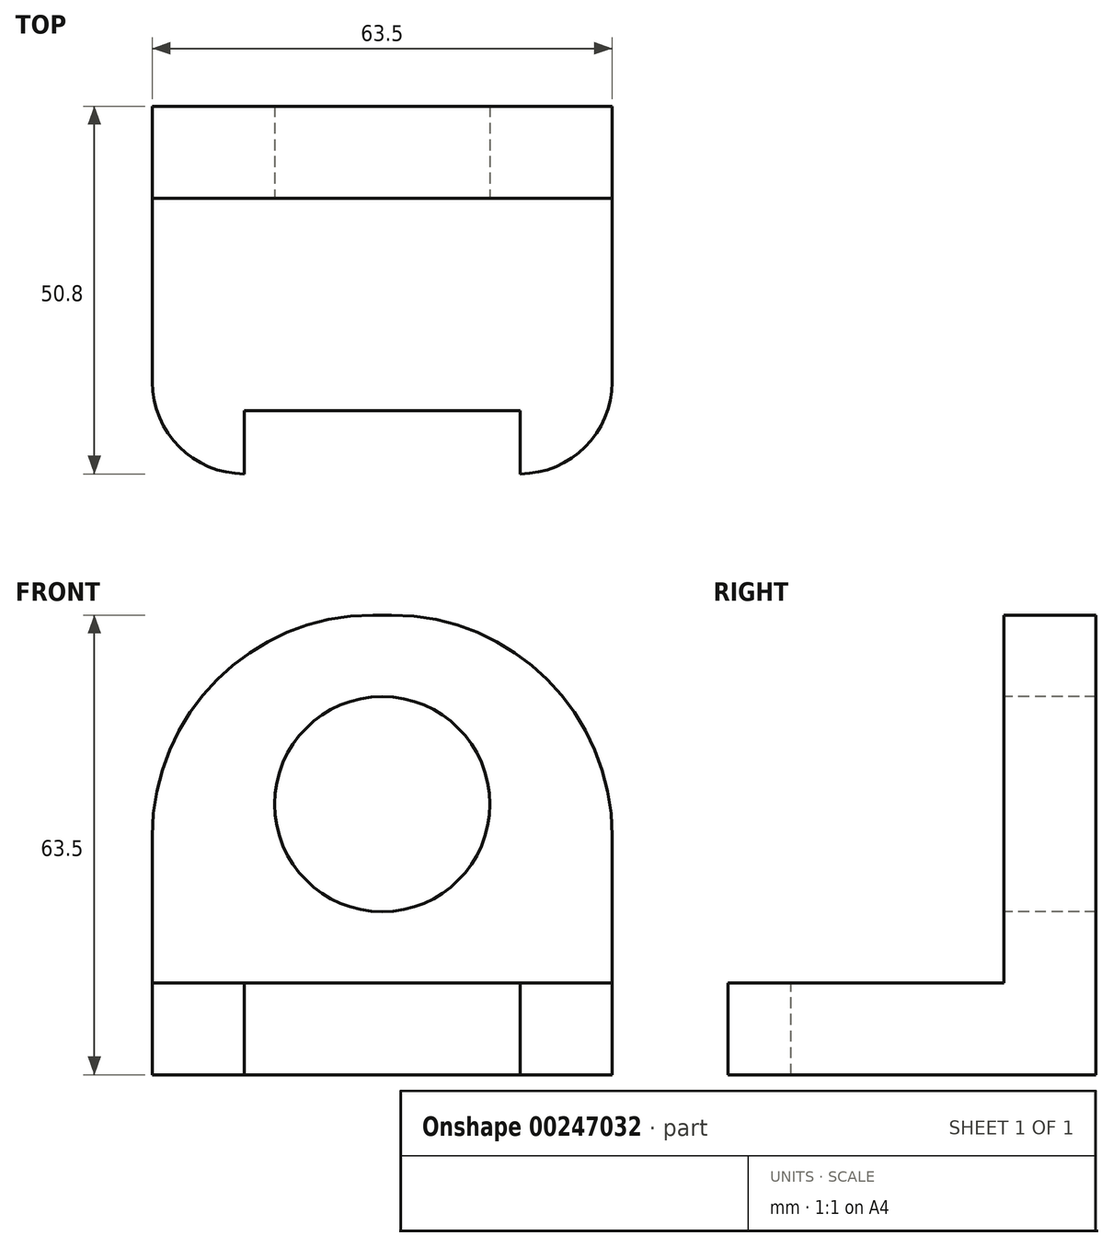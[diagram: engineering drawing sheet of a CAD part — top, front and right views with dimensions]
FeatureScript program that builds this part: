
annotation { "Feature Type Name" : "Feature", "Feature Type Description" : "" }
export const myFeature = defineFeature(function(context is Context, id is Id, definition is map)
    precondition{}
    {
        {
            var Q0;
            Q0=qCreatedBy(makeId("Right.planeOp"),FACE);
            var sketch = newSketch(context, id + "F0", { "sketchPlane" : qUnion([Q0])});
            skLineSegment(sketch, "E0", {"start": v(0, 0) * mm, "end": v(0, 63.5) * mm});
            skLineSegment(sketch, "E1", {"start": v(0, 63.5) * mm, "end": v(-12.7, 63.5) * mm});
            skLineSegment(sketch, "E2", {"start": v(-12.7, 63.5) * mm, "end": v(-12.7, 12.7) * mm});
            skLineSegment(sketch, "E3", {"start": v(-12.7, 12.7) * mm, "end": v(-50.8, 12.7) * mm});
            skLineSegment(sketch, "E4", {"start": v(-50.8, 12.7) * mm, "end": v(-50.8, 0) * mm});
            skLineSegment(sketch, "E5", {"start": v(-50.8, 0) * mm, "end": v(0, 0) * mm});
            skSolve(sketch);
        }
        {
            var Q0;
            Q0=makeQuery(id+"F0.imprint","IMPRINT",FACE,{"disambiguationData":[TD([[makeQuery(id+"F0.imprint","IMPRINT",EDGE,{"derivedFrom":sQuery(id+"F0.wireOp",EDGE,"E0")}),1.0]])]});
            extrude(context, id + "F1", {"entities" : qUnion([Q0]), "endBound" : BoundingType.SYMMETRIC, "depth" : 63.5 * mm});
        }
        {
            var Q0;
            Q0=makeQuery(id+"F1.opExtrude","SWEPT_FACE",FACE,{"disambiguationData":[OSD([sQuery(id+"F0.wireOp",EDGE,"E3")])]});
            var sketch = newSketch(context, id + "F2", { "sketchPlane" : qUnion([Q0])});
            skLineSegment(sketch, "E6.0", {"start": v(-31.75, -12.7) * mm, "end": v(-31.75, -38.1) * mm});
            skLineSegment(sketch, "E7.0", {"start": v(19.05, -50.8) * mm, "end": v(-19.05, -50.8) * mm});
            skLineSegment(sketch, "E8.0", {"start": v(31.75, -12.7) * mm, "end": v(31.75, -38.1) * mm});
            skPoint(sketch, "E9.visualSharp", {"position": v(-31.75, -50.8) * mm});
            skArc(sketch, "E9.filletArc", {"start": v(-31.75, -38.1) * mm, "mid": v(-28.03, -47.08) * mm, "end": v(-19.05, -50.8) * mm});
            skPoint(sketch, "E10.visualSharp", {"position": v(31.75, -50.8) * mm});
            skArc(sketch, "E10.filletArc", {"start": v(19.05, -50.8) * mm, "mid": v(28.03, -47.08) * mm, "end": v(31.75, -38.1) * mm});
            skSolve(sketch);
        }
        {
            var Q0;
            {var subQ0=sQuery(id+"F2.wireOp",EDGE,"E9.filletArc");Q0=makeQuery(id+"F2.imprint","IMPRINT",FACE,{"disambiguationData":[TD([[makeQuery(id+"F2.imprint","IMPRINT",EDGE,{"derivedFrom":subQ0}),-1.0]])]});}
            var Q1;
            {var subQ0=sQuery(id+"F2.wireOp",EDGE,"E10.filletArc");Q1=makeQuery(id+"F2.imprint","IMPRINT",FACE,{"disambiguationData":[TD([[makeQuery(id+"F2.imprint","IMPRINT",EDGE,{"derivedFrom":subQ0}),-1.0]])]});}
            extrude(context, id + "F3", {"entities" : qUnion([Q0, Q1]), "operationType" : NewBodyOperationType.REMOVE, "oppositeDirection" : true, "depth" : 25.4 * mm});
        }
        {
            var Q0;
            Q0=makeQuery(id+"F1.opExtrude","SWEPT_FACE",FACE,{"disambiguationData":[OSD([sQuery(id+"F0.wireOp",EDGE,"E3")])]});
            var sketch = newSketch(context, id + "F4", { "sketchPlane" : qUnion([Q0])});
            skLineSegment(sketch, "E11.bottom", {"start": v(-19.05, -50.8) * mm, "end": v(19.05, -50.8) * mm});
            skLineSegment(sketch, "E11.top", {"start": v(-19.05, -42.08) * mm, "end": v(19.05, -42.08) * mm});
            skLineSegment(sketch, "E11.left", {"start": v(-19.05, -50.8) * mm, "end": v(-19.05, -42.08) * mm});
            skLineSegment(sketch, "E11.right", {"start": v(19.05, -50.8) * mm, "end": v(19.05, -42.08) * mm});
            skSolve(sketch);
        }
        {
            var Q0;
            Q0=makeQuery(id+"F4.imprint","IMPRINT",FACE,{"disambiguationData":[TD([[makeQuery(id+"F4.imprint","IMPRINT",EDGE,{"derivedFrom":sQuery(id+"F4.wireOp",EDGE,"E11.bottom")}),-1.0]])]});
            extrude(context, id + "F5", {"entities" : qUnion([Q0]), "operationType" : NewBodyOperationType.REMOVE, "oppositeDirection" : true, "depth" : 25.4 * mm});
        }
        {
            var Q0;
            Q0=makeQuery(id+"F1.opExtrude","SWEPT_FACE",FACE,{"disambiguationData":[OSD([sQuery(id+"F0.wireOp",EDGE,"E2")])]});
            var sketch = newSketch(context, id + "F6", { "sketchPlane" : qUnion([Q0])});
            skLineSegment(sketch, "E12.0", {"start": v(-31.75, 33.02) * mm, "end": v(-31.75, 12.7) * mm});
            skLineSegment(sketch, "E13.0", {"start": v(1.27, 63.5) * mm, "end": v(-1.27, 63.5) * mm});
            skLineSegment(sketch, "E14.0", {"start": v(31.75, 33.02) * mm, "end": v(31.75, 12.7) * mm});
            skPoint(sketch, "E15.visualSharp", {"position": v(-31.75, 63.5) * mm});
            skArc(sketch, "E15.filletArc", {"start": v(-1.27, 63.5) * mm, "mid": v(-22.82, 54.57) * mm, "end": v(-31.75, 33.02) * mm});
            skPoint(sketch, "E16.visualSharp", {"position": v(31.75, 63.5) * mm});
            skArc(sketch, "E16.filletArc", {"start": v(31.75, 33.02) * mm, "mid": v(22.82, 54.57) * mm, "end": v(1.27, 63.5) * mm});
            skCircle(sketch, "E17", {"center": v(0, 37.37) * mm, "radius": 14.86 * mm});
            skSolve(sketch);
        }
        {
            var Q0;
            {var subQ0=sQuery(id+"F6.wireOp",EDGE,"E15.filletArc");Q0=makeQuery(id+"F6.imprint","IMPRINT",FACE,{"disambiguationData":[TD([[makeQuery(id+"F6.imprint","IMPRINT",EDGE,{"derivedFrom":subQ0}),-1.0]])]});}
            var Q1;
            {var subQ0=sQuery(id+"F6.wireOp",EDGE,"E16.filletArc");Q1=makeQuery(id+"F6.imprint","IMPRINT",FACE,{"disambiguationData":[TD([[makeQuery(id+"F6.imprint","IMPRINT",EDGE,{"derivedFrom":subQ0}),-1.0]])]});}
            var Q2;
            Q2=makeQuery(id+"F6.imprint","IMPRINT",FACE,{"disambiguationData":[TD([[makeQuery(id+"F6.imprint","IMPRINT",EDGE,{"derivedFrom":sQuery(id+"F6.wireOp",EDGE,"E17")}),1.0]])]});
            extrude(context, id + "F7", {"entities" : qUnion([Q0, Q1, Q2]), "operationType" : NewBodyOperationType.REMOVE, "oppositeDirection" : true, "depth" : 25.4 * mm});
        }
    });
